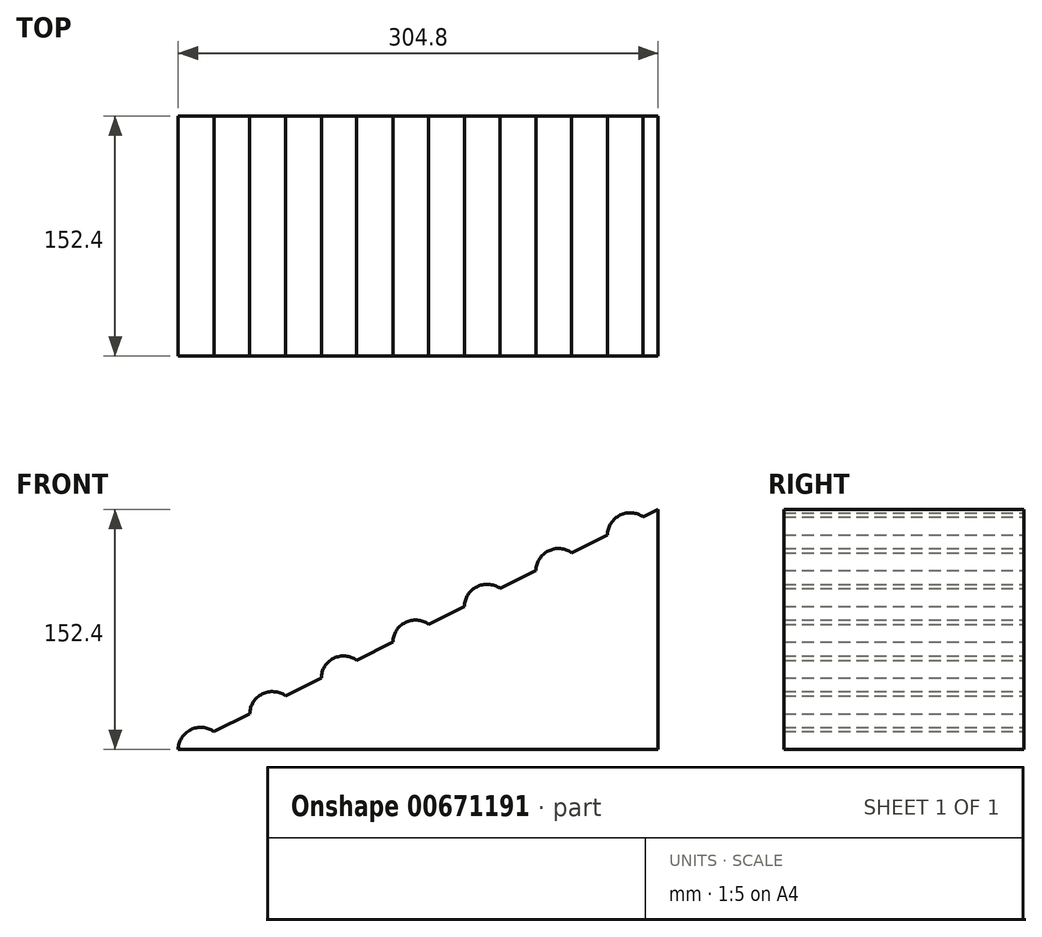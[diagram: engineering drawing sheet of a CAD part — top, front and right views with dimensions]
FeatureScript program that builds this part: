
annotation { "Feature Type Name" : "Feature", "Feature Type Description" : "" }
export const myFeature = defineFeature(function(context is Context, id is Id, definition is map)
    precondition{}
    {
        {
            var Q0;
            Q0=qCreatedBy(makeId("Front.planeOp"),FACE);
            var sketch = newSketch(context, id + "F0", { "sketchPlane" : qUnion([Q0])});
            skLineSegment(sketch, "E0", {"start": v(180.64, 0) * mm, "end": v(-124.16, 0) * mm});
            skLineSegment(sketch, "E1", {"start": v(-124.16, 0) * mm, "end": v(180.64, 152.4) * mm});
            skLineSegment(sketch, "E2", {"start": v(180.64, 152.4) * mm, "end": v(180.64, 0) * mm});
            skArc(sketch, "E3", {"start": v(-101.44, 11.36) * mm, "mid": v(-116.2, 12.5) * mm, "end": v(-124.16, 0) * mm});
            skArc(sketch, "E4", {"start": v(-56, 34.08) * mm, "mid": v(-70.77, 35.21) * mm, "end": v(-78.72, 22.72) * mm});
            skArc(sketch, "E5", {"start": v(-10.3, 56.25) * mm, "mid": v(-25.16, 58.01) * mm, "end": v(-33.28, 45.44) * mm});
            skArc(sketch, "E6", {"start": v(34.86, 79.5) * mm, "mid": v(20.1, 80.64) * mm, "end": v(12.14, 68.15) * mm});
            skArc(sketch, "E7", {"start": v(80.3, 102.23) * mm, "mid": v(65.53, 103.36) * mm, "end": v(57.58, 90.87) * mm});
            skArc(sketch, "E8", {"start": v(125.73, 124.94) * mm, "mid": v(110.97, 126.08) * mm, "end": v(103.02, 113.59) * mm});
            skArc(sketch, "E9", {"start": v(171.17, 147.66) * mm, "mid": v(156.4, 148.8) * mm, "end": v(148.45, 136.3) * mm});
            skSolve(sketch);
        }
        {
            var Q0;
            {var subQ0=sQuery(id+"F0.wireOp",EDGE,"E9");Q0=makeQuery(id+"F0.imprint","IMPRINT",FACE,{"disambiguationData":[TD([[makeQuery(id+"F0.imprint","IMPRINT",EDGE,{"derivedFrom":subQ0}),1.0]])]});}
            var Q1;
            {var subQ0=sQuery(id+"F0.wireOp",EDGE,"E8");Q1=makeQuery(id+"F0.imprint","IMPRINT",FACE,{"disambiguationData":[TD([[makeQuery(id+"F0.imprint","IMPRINT",EDGE,{"derivedFrom":subQ0}),1.0]])]});}
            var Q2;
            {var subQ0=sQuery(id+"F0.wireOp",EDGE,"E7");Q2=makeQuery(id+"F0.imprint","IMPRINT",FACE,{"disambiguationData":[TD([[makeQuery(id+"F0.imprint","IMPRINT",EDGE,{"derivedFrom":subQ0}),1.0]])]});}
            var Q3;
            {var subQ0=sQuery(id+"F0.wireOp",EDGE,"E6");Q3=makeQuery(id+"F0.imprint","IMPRINT",FACE,{"disambiguationData":[TD([[makeQuery(id+"F0.imprint","IMPRINT",EDGE,{"derivedFrom":subQ0}),1.0]])]});}
            var Q4;
            {var subQ0=sQuery(id+"F0.wireOp",EDGE,"E5");Q4=makeQuery(id+"F0.imprint","IMPRINT",FACE,{"disambiguationData":[TD([[makeQuery(id+"F0.imprint","IMPRINT",EDGE,{"derivedFrom":subQ0}),1.0]])]});}
            var Q5;
            {var subQ12=sQuery(id+"F0.wireOp",EDGE,"E0");Q5=makeQuery(id+"F0.imprint","IMPRINT",FACE,{"disambiguationData":[TD([[makeQuery(id+"F0.imprint","IMPRINT",EDGE,{"derivedFrom":subQ12}),-1.0]])]});}
            var Q6;
            {var subQ0=sQuery(id+"F0.wireOp",EDGE,"E4");Q6=makeQuery(id+"F0.imprint","IMPRINT",FACE,{"disambiguationData":[TD([[makeQuery(id+"F0.imprint","IMPRINT",EDGE,{"derivedFrom":subQ0}),1.0]])]});}
            var Q7;
            {var subQ0=sQuery(id+"F0.wireOp",EDGE,"E3");Q7=makeQuery(id+"F0.imprint","IMPRINT",FACE,{"disambiguationData":[TD([[makeQuery(id+"F0.imprint","IMPRINT",EDGE,{"derivedFrom":subQ0}),1.0]])]});}
            extrude(context, id + "F1", {"entities" : qUnion([Q0, Q1, Q2, Q3, Q4, Q5, Q6, Q7]), "endBound" : BoundingType.SYMMETRIC, "depth" : 152.4 * mm, "offsetDistance" : 25.4 * mm});
        }
    });
